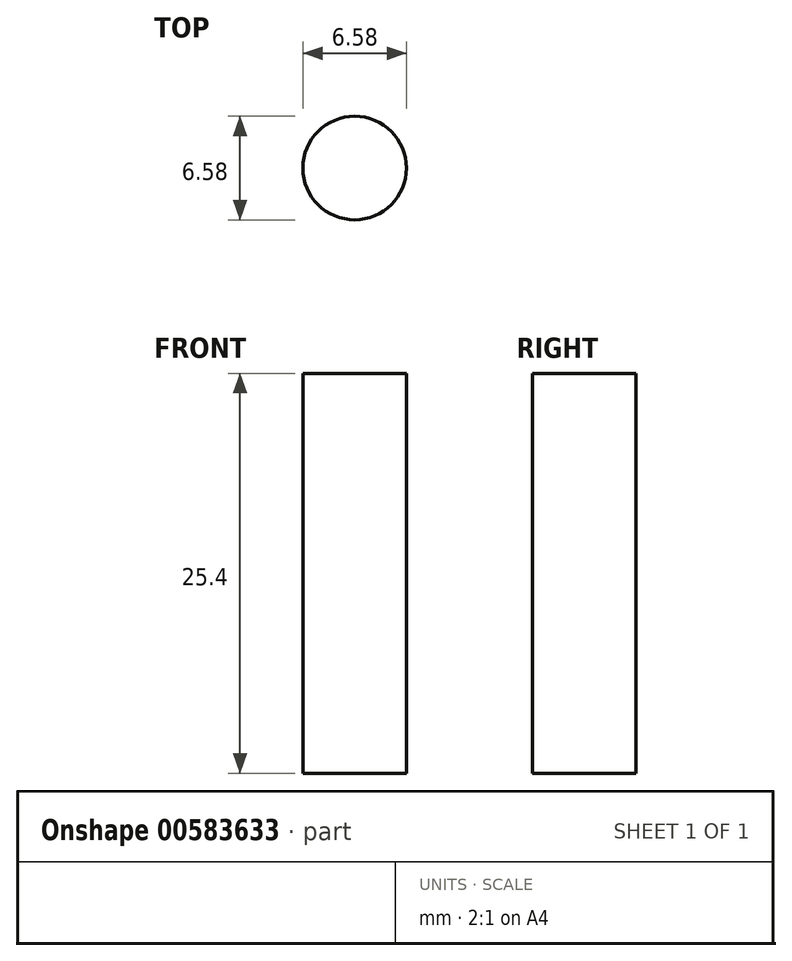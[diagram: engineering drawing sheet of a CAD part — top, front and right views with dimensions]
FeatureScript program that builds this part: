
annotation { "Feature Type Name" : "Feature", "Feature Type Description" : "" }
export const myFeature = defineFeature(function(context is Context, id is Id, definition is map)
    precondition{}
    {
        {
            var Q0;
            Q0=qCreatedBy(makeId("Top.planeOp"),FACE);
            var sketch = newSketch(context, id + "F0", { "sketchPlane" : qUnion([Q0])});
            skCircle(sketch, "E0", {"center": v(0, 0) * mm, "radius": 3.29 * mm});
            skSolve(sketch);
        }
        {
            var Q0;
            Q0=makeQuery(id+"F0.imprint","IMPRINT",FACE,{"disambiguationData":[TD([[makeQuery(id+"F0.imprint","IMPRINT",EDGE,{"derivedFrom":sQuery(id+"F0.wireOp",EDGE,"E0")}),1.0]])]});
            extrude(context, id + "F1", {"entities" : qUnion([Q0]), "depth" : 25.4 * mm, "offsetDistance" : 25.4 * mm});
        }
    });
